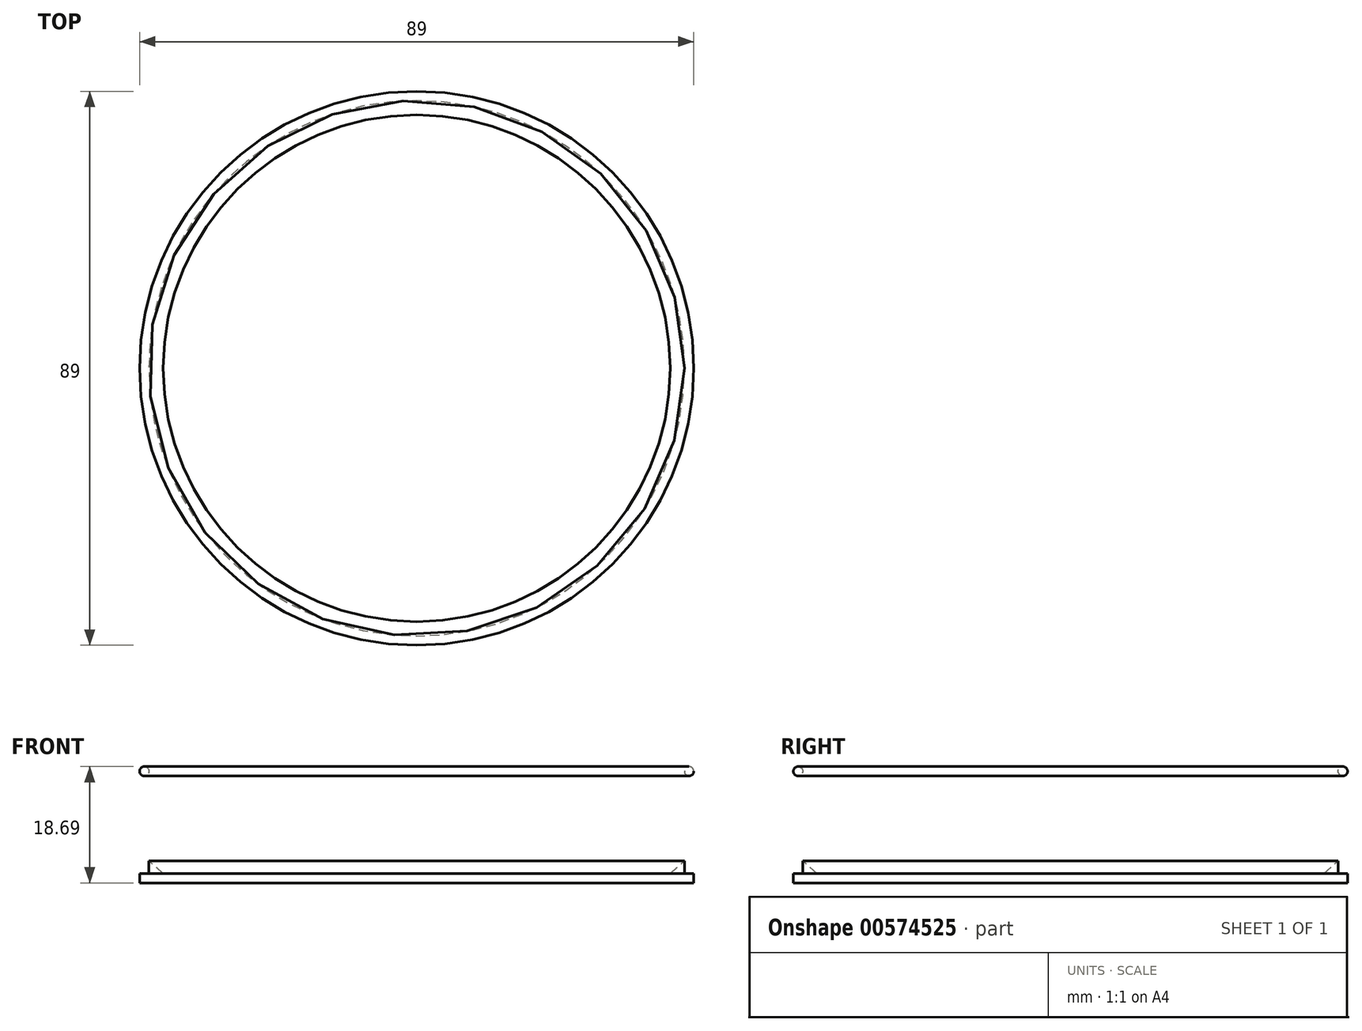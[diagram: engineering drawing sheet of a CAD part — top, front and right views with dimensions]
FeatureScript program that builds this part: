
annotation { "Feature Type Name" : "Feature", "Feature Type Description" : "" }
export const myFeature = defineFeature(function(context is Context, id is Id, definition is map)
    precondition{}
    {
        {
            var Q0;
            Q0=qCreatedBy(makeId("Front.planeOp"),FACE);
            var sketch = newSketch(context, id + "F0", { "sketchPlane" : qUnion([Q0])});
            skLineSegment(sketch, "E0.bottom", {"start": v(0, 1.5) * mm, "end": v(44.5, 1.5) * mm});
            skLineSegment(sketch, "E0.top", {"start": v(0, 0) * mm, "end": v(44.5, 0) * mm});
            skLineSegment(sketch, "E0.left", {"start": v(0, 1.5) * mm, "end": v(0, 0) * mm});
            skLineSegment(sketch, "E0.right", {"start": v(44.5, 1.5) * mm, "end": v(44.5, 0) * mm});
            skLineSegment(sketch, "E1.bottom", {"start": v(43, 18) * mm, "end": v(44.5, 18) * mm});
            skLineSegment(sketch, "E1.top", {"start": v(43, 1.5) * mm, "end": v(44.5, 1.5) * mm});
            skLineSegment(sketch, "E1.left", {"start": v(43, 18) * mm, "end": v(43, 1.5) * mm});
            skLineSegment(sketch, "E1.right", {"start": v(44.5, 18) * mm, "end": v(44.5, 1.5) * mm});
            skLineSegment(sketch, "E2", {"start": v(43, 3.53) * mm, "end": v(40.71, 1.5) * mm});
            skLineSegment(sketch, "E3", {"start": v(0, 30.57) * mm, "end": v(0, -32.23) * mm});
            skCircle(sketch, "E4", {"center": v(43.75, 17.94) * mm, "radius": 0.75 * mm});
            skPoint(sketch, "E4.third.point", {"position": v(44.5, 18) * mm});
            skSolve(sketch);
        }
        {
            var Q0;
            {var subQ0=sQuery(id+"F0.wireOp",EDGE,"E0.top");Q0=makeQuery(id+"F0.imprint","IMPRINT",FACE,{"disambiguationData":[TD([[makeQuery(id+"F0.imprint","IMPRINT",EDGE,{"derivedFrom":subQ0}),1.0]])]});}
            var Q1;
            {var subQ1=sQuery(id+"F0.wireOp",EDGE,"E1.top");Q1=makeQuery(id+"F0.imprint","IMPRINT",FACE,{"disambiguationData":[TD([[makeQuery(id+"F0.imprint","IMPRINT",EDGE,{"derivedFrom":subQ1}),1.0]])]});}
            var Q2;
            {var subQ3=sQuery(id+"F0.wireOp",EDGE,"E2");Q2=makeQuery(id+"F0.imprint","IMPRINT",FACE,{"disambiguationData":[TD([[makeQuery(id+"F0.imprint","IMPRINT",EDGE,{"derivedFrom":subQ3}),1.0]])]});}
            var Q3;
            {var subQ0=sQuery(id+"F0.wireOp",EDGE,"E1.bottom");Q3=makeQuery(id+"F0.imprint","IMPRINT",FACE,{"disambiguationData":[TD([[makeQuery(id+"F0.imprint","IMPRINT",EDGE,{"derivedFrom":subQ0}),1.0]])]});}
            var Q4;
            {var subQ0=sQuery(id+"F0.wireOp",EDGE,"E1.bottom");Q4=makeQuery(id+"F0.imprint","IMPRINT",FACE,{"disambiguationData":[TD([[makeQuery(id+"F0.imprint","IMPRINT",EDGE,{"derivedFrom":subQ0}),-1.0]])]});}
            var Q5;
            {var subQ0=sQuery(id+"F0.wireOp",EDGE,"E4");var subQ1=sQuery(id+"F0.wireOp",EDGE,"E1.right");var subQ3=makeQuery(id+"F0.imprint","INTERSECT",VERTEX,{"derivedFrom":[subQ1,subQ0]});Q5=makeQuery(id+"F0.imprint","IMPRINT",FACE,{"disambiguationData":[TD([[makeQuery(id+"F0.imprint","IMPRINT",EDGE,{"disambiguationData":[TD([[subQ3,1.0]])],"derivedFrom":subQ1}),1.0]])]});}
            var Q6;
            {var subQ0=sQuery(id+"F0.wireOp",EDGE,"E4");var subQ1=sQuery(id+"F0.wireOp",EDGE,"E1.left");var subQ3=makeQuery(id+"F0.imprint","INTERSECT",VERTEX,{"derivedFrom":[subQ1,subQ0]});Q6=makeQuery(id+"F0.imprint","IMPRINT",FACE,{"disambiguationData":[TD([[makeQuery(id+"F0.imprint","IMPRINT",EDGE,{"disambiguationData":[TD([[subQ3,1.0]])],"derivedFrom":subQ1}),-1.0]])]});}
            var Q7;
            Q7=sQuery(id+"F0.wireOp",EDGE,"E3");
            revolve(context, id + "F1", {"entities" : qUnion([Q0, Q1, Q2, Q3, Q4, Q5, Q6]), "axis" : qUnion([Q7]), "revolveType" : RevolveType.FULL});
        }
    });
